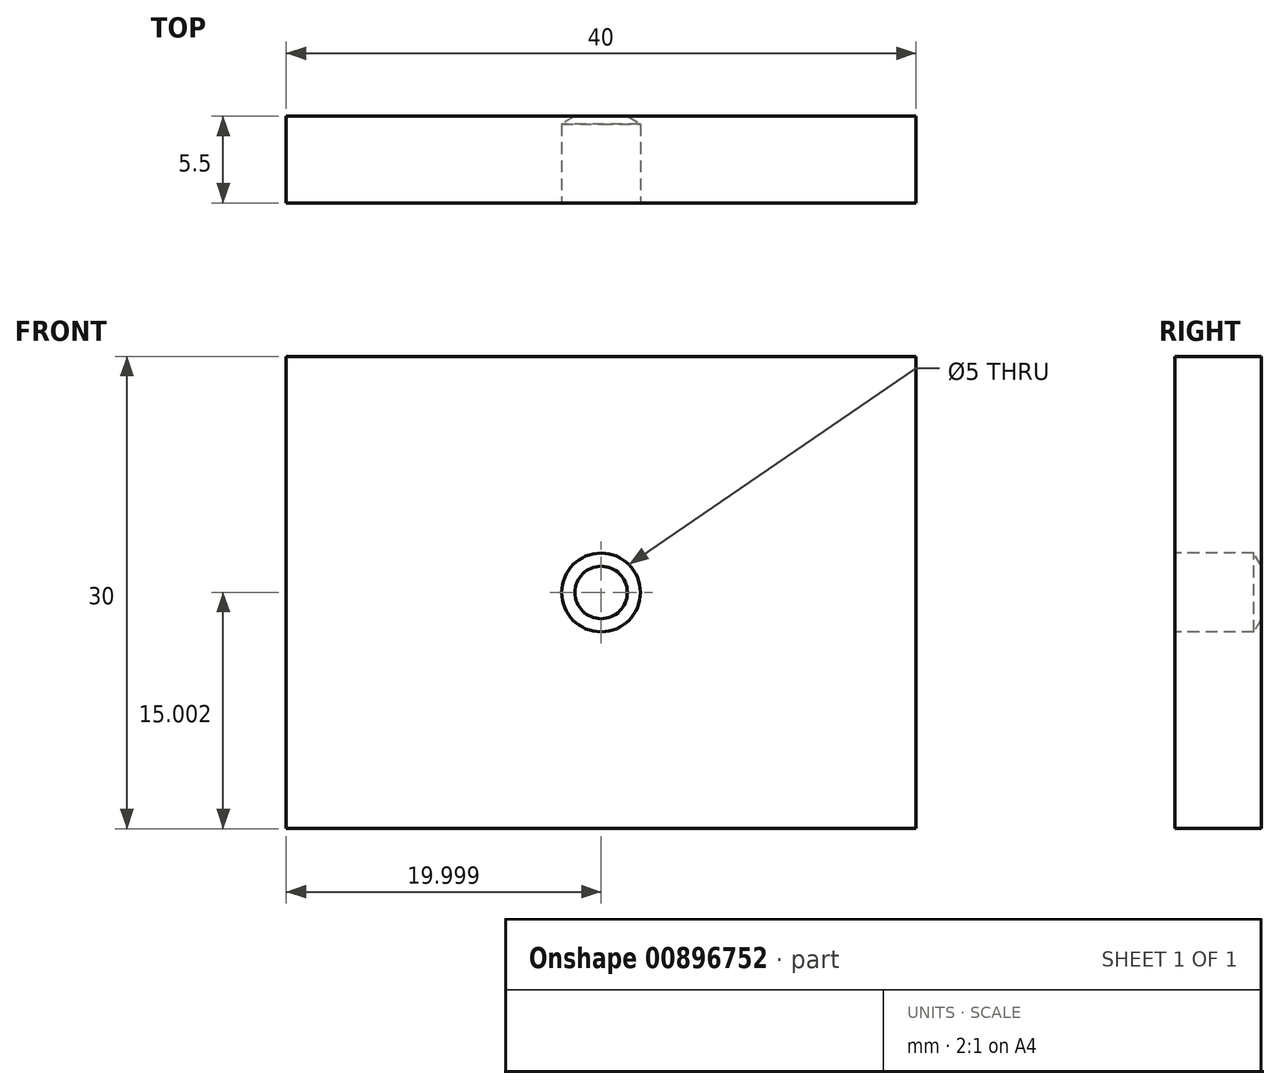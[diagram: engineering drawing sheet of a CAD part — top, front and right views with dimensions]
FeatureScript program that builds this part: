
annotation { "Feature Type Name" : "Feature", "Feature Type Description" : "" }
export const myFeature = defineFeature(function(context is Context, id is Id, definition is map)
    precondition{}
    {
        {
            var Q0;
            Q0=qCreatedBy(makeId("Front.planeOp"),FACE);
            var sketch = newSketch(context, id + "F0", { "sketchPlane" : qUnion([Q0])});
            skLineSegment(sketch, "E0.bottom", {"start": v(20.84, -8.05) * mm, "end": v(60.84, -8.05) * mm});
            skLineSegment(sketch, "E0.top", {"start": v(20.84, -38.05) * mm, "end": v(60.84, -38.05) * mm});
            skLineSegment(sketch, "E0.left", {"start": v(20.84, -8.05) * mm, "end": v(20.84, -38.05) * mm});
            skLineSegment(sketch, "E0.right", {"start": v(60.84, -8.05) * mm, "end": v(60.84, -38.05) * mm});
            skSolve(sketch);
        }
        {
            var Q0;
            Q0=makeQuery(id+"F0.imprint","IMPRINT",FACE,{"disambiguationData":[TD([[makeQuery(id+"F0.imprint","IMPRINT",EDGE,{"derivedFrom":sQuery(id+"F0.wireOp",EDGE,"E0.bottom")}),-1.0]])]});
            extrude(context, id + "F1", {"entities" : qUnion([Q0]), "depth" : 5.5 * mm, "offsetDistance" : 25 * mm});
        }
        {
            var Q0;
            Q0=makeQuery(id+"F1.opExtrude","CAP_FACE",FACE,{"disambiguationData":[OSD([sQuery(id+"F0.wireOp",EDGE,"E0.bottom"),sQuery(id+"F0.wireOp",EDGE,"E0.top"),sQuery(id+"F0.wireOp",EDGE,"E0.left"),sQuery(id+"F0.wireOp",EDGE,"E0.right")])],"isStart":false});
            var sketch = newSketch(context, id + "F2", { "sketchPlane" : qUnion([Q0])});
            skLineSegment(sketch, "E1", {"start": v(40.84, -8.05) * mm, "end": v(40.84, -38.05) * mm});
            skLineSegment(sketch, "E2", {"start": v(20.84, -23.05) * mm, "end": v(60.84, -23.05) * mm});
            skLineSegment(sketch, "E3", {"start": v(40.84, -23.05) * mm, "end": v(20.84, -23.05) * mm});
            skSolve(sketch);
        }
        {
            var Q0;
            Q0=sQuery(id+"F2.wireOp",VERTEX,"E3.start");
            var Q1;
            Q1=makeQuery(id+"F1.opExtrude","SWEPT_BODY",BODY,{"disambiguationData":[OSD([sQuery(id+"F0.wireOp",EDGE,"E0.bottom"),sQuery(id+"F0.wireOp",EDGE,"E0.top"),sQuery(id+"F0.wireOp",EDGE,"E0.left"),sQuery(id+"F0.wireOp",EDGE,"E0.right")])]});
            hole(context, id + "F3", {"style" : HoleStyle.SIMPLE, "endStyle" : HoleEndStyle.BLIND, "holeDiameter" : 5 * mm, "majorDiameter" : 5 * mm, "holeDepth" : 5 * mm, "isTappedThrough" : true, "tappedDepth" : 12 * mm, "tapClearance" : 3, "locations" : qUnion([Q0]), "scope" : qUnion([Q1])});
        }
    });
